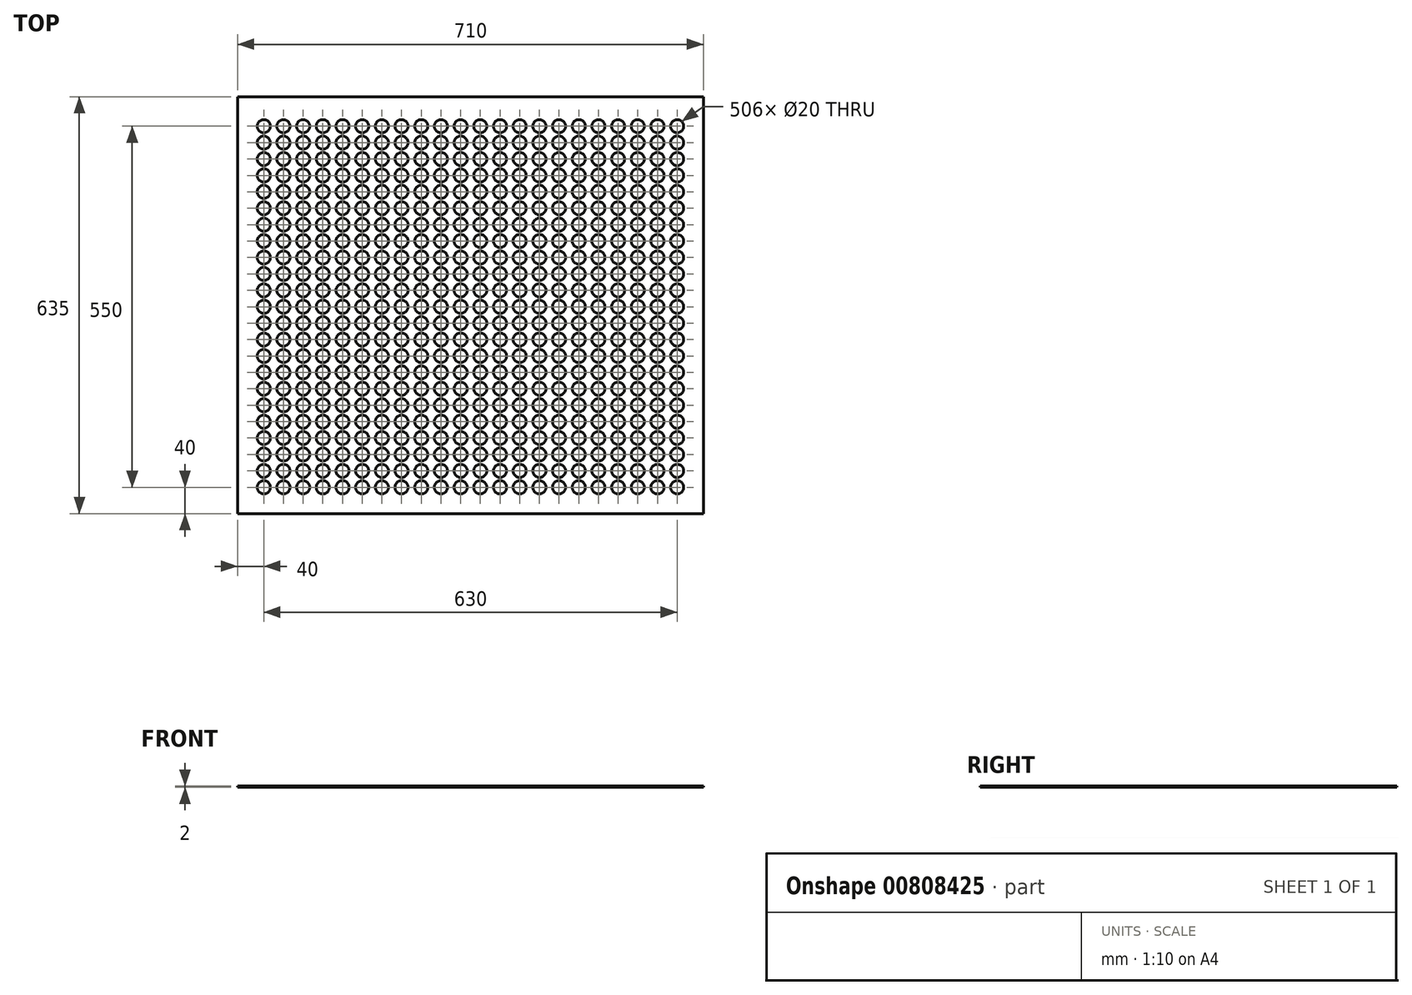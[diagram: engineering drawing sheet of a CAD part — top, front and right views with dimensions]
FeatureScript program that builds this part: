
annotation { "Feature Type Name" : "Feature", "Feature Type Description" : "" }
export const myFeature = defineFeature(function(context is Context, id is Id, definition is map)
    precondition{}
    {
        {
            var Q0;
            Q0=qCreatedBy(makeId("Top.planeOp"),FACE);
            var sketch = newSketch(context, id + "F0", { "sketchPlane" : qUnion([Q0])});
            skLineSegment(sketch, "E0.bottom", {"start": v(-355, 317.5) * mm, "end": v(355, 317.5) * mm});
            skLineSegment(sketch, "E0.top", {"start": v(-355, -317.5) * mm, "end": v(355, -317.5) * mm});
            skLineSegment(sketch, "E0.left", {"start": v(-355, 317.5) * mm, "end": v(-355, -317.5) * mm});
            skLineSegment(sketch, "E0.right", {"start": v(355, 317.5) * mm, "end": v(355, -317.5) * mm});
            skPoint(sketch, "E0.middle", {"position": v(0, 0) * mm});
            skCircle(sketch, "E1", {"center": v(-315, -277.5) * mm, "radius": 10 * mm});
            skCircle(sketch, "E2.0.1.0", {"center": v(-315, -252.5) * mm, "radius": 10 * mm});
            skCircle(sketch, "E2.0.2.0", {"center": v(-315, -227.5) * mm, "radius": 10 * mm});
            skCircle(sketch, "E2.0.3.0", {"center": v(-315, -202.5) * mm, "radius": 10 * mm});
            skCircle(sketch, "E2.0.4.0", {"center": v(-315, -177.5) * mm, "radius": 10 * mm});
            skCircle(sketch, "E2.0.5.0", {"center": v(-315, -152.5) * mm, "radius": 10 * mm});
            skCircle(sketch, "E2.0.6.0", {"center": v(-315, -127.5) * mm, "radius": 10 * mm});
            skCircle(sketch, "E2.0.7.0", {"center": v(-315, -102.5) * mm, "radius": 10 * mm});
            skCircle(sketch, "E2.0.8.0", {"center": v(-315, -77.5) * mm, "radius": 10 * mm});
            skCircle(sketch, "E2.0.9.0", {"center": v(-315, -52.5) * mm, "radius": 10 * mm});
            skCircle(sketch, "E2.1.0.0", {"center": v(-285, -277.5) * mm, "radius": 10 * mm});
            skCircle(sketch, "E2.1.1.0", {"center": v(-285, -252.5) * mm, "radius": 10 * mm});
            skCircle(sketch, "E2.1.2.0", {"center": v(-285, -227.5) * mm, "radius": 10 * mm});
            skCircle(sketch, "E2.1.3.0", {"center": v(-285, -202.5) * mm, "radius": 10 * mm});
            skCircle(sketch, "E2.1.4.0", {"center": v(-285, -177.5) * mm, "radius": 10 * mm});
            skCircle(sketch, "E2.1.5.0", {"center": v(-285, -152.5) * mm, "radius": 10 * mm});
            skCircle(sketch, "E2.1.6.0", {"center": v(-285, -127.5) * mm, "radius": 10 * mm});
            skCircle(sketch, "E2.1.7.0", {"center": v(-285, -102.5) * mm, "radius": 10 * mm});
            skCircle(sketch, "E2.1.8.0", {"center": v(-285, -77.5) * mm, "radius": 10 * mm});
            skCircle(sketch, "E2.1.9.0", {"center": v(-285, -52.5) * mm, "radius": 10 * mm});
            skCircle(sketch, "E2.2.0.0", {"center": v(-255, -277.5) * mm, "radius": 10 * mm});
            skCircle(sketch, "E2.2.1.0", {"center": v(-255, -252.5) * mm, "radius": 10 * mm});
            skCircle(sketch, "E2.2.2.0", {"center": v(-255, -227.5) * mm, "radius": 10 * mm});
            skCircle(sketch, "E2.2.3.0", {"center": v(-255, -202.5) * mm, "radius": 10 * mm});
            skCircle(sketch, "E2.2.4.0", {"center": v(-255, -177.5) * mm, "radius": 10 * mm});
            skCircle(sketch, "E2.2.5.0", {"center": v(-255, -152.5) * mm, "radius": 10 * mm});
            skCircle(sketch, "E2.2.6.0", {"center": v(-255, -127.5) * mm, "radius": 10 * mm});
            skCircle(sketch, "E2.2.7.0", {"center": v(-255, -102.5) * mm, "radius": 10 * mm});
            skCircle(sketch, "E2.2.8.0", {"center": v(-255, -77.5) * mm, "radius": 10 * mm});
            skCircle(sketch, "E2.2.9.0", {"center": v(-255, -52.5) * mm, "radius": 10 * mm});
            skCircle(sketch, "E2.3.0.0", {"center": v(-225, -277.5) * mm, "radius": 10 * mm});
            skCircle(sketch, "E2.3.1.0", {"center": v(-225, -252.5) * mm, "radius": 10 * mm});
            skCircle(sketch, "E2.3.2.0", {"center": v(-225, -227.5) * mm, "radius": 10 * mm});
            skCircle(sketch, "E2.3.3.0", {"center": v(-225, -202.5) * mm, "radius": 10 * mm});
            skCircle(sketch, "E2.3.4.0", {"center": v(-225, -177.5) * mm, "radius": 10 * mm});
            skCircle(sketch, "E2.3.5.0", {"center": v(-225, -152.5) * mm, "radius": 10 * mm});
            skCircle(sketch, "E2.3.6.0", {"center": v(-225, -127.5) * mm, "radius": 10 * mm});
            skCircle(sketch, "E2.3.7.0", {"center": v(-225, -102.5) * mm, "radius": 10 * mm});
            skCircle(sketch, "E2.3.8.0", {"center": v(-225, -77.5) * mm, "radius": 10 * mm});
            skCircle(sketch, "E2.3.9.0", {"center": v(-225, -52.5) * mm, "radius": 10 * mm});
            skCircle(sketch, "E2.4.0.0", {"center": v(-195, -277.5) * mm, "radius": 10 * mm});
            skCircle(sketch, "E2.4.1.0", {"center": v(-195, -252.5) * mm, "radius": 10 * mm});
            skCircle(sketch, "E2.4.2.0", {"center": v(-195, -227.5) * mm, "radius": 10 * mm});
            skCircle(sketch, "E2.4.3.0", {"center": v(-195, -202.5) * mm, "radius": 10 * mm});
            skCircle(sketch, "E2.4.4.0", {"center": v(-195, -177.5) * mm, "radius": 10 * mm});
            skCircle(sketch, "E2.4.5.0", {"center": v(-195, -152.5) * mm, "radius": 10 * mm});
            skCircle(sketch, "E2.4.6.0", {"center": v(-195, -127.5) * mm, "radius": 10 * mm});
            skCircle(sketch, "E2.4.7.0", {"center": v(-195, -102.5) * mm, "radius": 10 * mm});
            skCircle(sketch, "E2.4.8.0", {"center": v(-195, -77.5) * mm, "radius": 10 * mm});
            skCircle(sketch, "E2.4.9.0", {"center": v(-195, -52.5) * mm, "radius": 10 * mm});
            skCircle(sketch, "E2.5.0.0", {"center": v(-165, -277.5) * mm, "radius": 10 * mm});
            skCircle(sketch, "E2.5.1.0", {"center": v(-165, -252.5) * mm, "radius": 10 * mm});
            skCircle(sketch, "E2.5.2.0", {"center": v(-165, -227.5) * mm, "radius": 10 * mm});
            skCircle(sketch, "E2.5.3.0", {"center": v(-165, -202.5) * mm, "radius": 10 * mm});
            skCircle(sketch, "E2.5.4.0", {"center": v(-165, -177.5) * mm, "radius": 10 * mm});
            skCircle(sketch, "E2.5.5.0", {"center": v(-165, -152.5) * mm, "radius": 10 * mm});
            skCircle(sketch, "E2.5.6.0", {"center": v(-165, -127.5) * mm, "radius": 10 * mm});
            skCircle(sketch, "E2.5.7.0", {"center": v(-165, -102.5) * mm, "radius": 10 * mm});
            skCircle(sketch, "E2.5.8.0", {"center": v(-165, -77.5) * mm, "radius": 10 * mm});
            skCircle(sketch, "E2.5.9.0", {"center": v(-165, -52.5) * mm, "radius": 10 * mm});
            skCircle(sketch, "E2.6.0.0", {"center": v(-135, -277.5) * mm, "radius": 10 * mm});
            skCircle(sketch, "E2.6.1.0", {"center": v(-135, -252.5) * mm, "radius": 10 * mm});
            skCircle(sketch, "E2.6.2.0", {"center": v(-135, -227.5) * mm, "radius": 10 * mm});
            skCircle(sketch, "E2.6.3.0", {"center": v(-135, -202.5) * mm, "radius": 10 * mm});
            skCircle(sketch, "E2.6.4.0", {"center": v(-135, -177.5) * mm, "radius": 10 * mm});
            skCircle(sketch, "E2.6.5.0", {"center": v(-135, -152.5) * mm, "radius": 10 * mm});
            skCircle(sketch, "E2.6.6.0", {"center": v(-135, -127.5) * mm, "radius": 10 * mm});
            skCircle(sketch, "E2.6.7.0", {"center": v(-135, -102.5) * mm, "radius": 10 * mm});
            skCircle(sketch, "E2.6.8.0", {"center": v(-135, -77.5) * mm, "radius": 10 * mm});
            skCircle(sketch, "E2.6.9.0", {"center": v(-135, -52.5) * mm, "radius": 10 * mm});
            skCircle(sketch, "E2.7.0.0", {"center": v(-105, -277.5) * mm, "radius": 10 * mm});
            skCircle(sketch, "E2.7.1.0", {"center": v(-105, -252.5) * mm, "radius": 10 * mm});
            skCircle(sketch, "E2.7.2.0", {"center": v(-105, -227.5) * mm, "radius": 10 * mm});
            skCircle(sketch, "E2.7.3.0", {"center": v(-105, -202.5) * mm, "radius": 10 * mm});
            skCircle(sketch, "E2.7.4.0", {"center": v(-105, -177.5) * mm, "radius": 10 * mm});
            skCircle(sketch, "E2.7.5.0", {"center": v(-105, -152.5) * mm, "radius": 10 * mm});
            skCircle(sketch, "E2.7.6.0", {"center": v(-105, -127.5) * mm, "radius": 10 * mm});
            skCircle(sketch, "E2.7.7.0", {"center": v(-105, -102.5) * mm, "radius": 10 * mm});
            skCircle(sketch, "E2.7.8.0", {"center": v(-105, -77.5) * mm, "radius": 10 * mm});
            skCircle(sketch, "E2.7.9.0", {"center": v(-105, -52.5) * mm, "radius": 10 * mm});
            skCircle(sketch, "E2.8.0.0", {"center": v(-75, -277.5) * mm, "radius": 10 * mm});
            skCircle(sketch, "E2.8.1.0", {"center": v(-75, -252.5) * mm, "radius": 10 * mm});
            skCircle(sketch, "E2.8.2.0", {"center": v(-75, -227.5) * mm, "radius": 10 * mm});
            skCircle(sketch, "E2.8.3.0", {"center": v(-75, -202.5) * mm, "radius": 10 * mm});
            skCircle(sketch, "E2.8.4.0", {"center": v(-75, -177.5) * mm, "radius": 10 * mm});
            skCircle(sketch, "E2.8.5.0", {"center": v(-75, -152.5) * mm, "radius": 10 * mm});
            skCircle(sketch, "E2.8.6.0", {"center": v(-75, -127.5) * mm, "radius": 10 * mm});
            skCircle(sketch, "E2.8.7.0", {"center": v(-75, -102.5) * mm, "radius": 10 * mm});
            skCircle(sketch, "E2.8.8.0", {"center": v(-75, -77.5) * mm, "radius": 10 * mm});
            skCircle(sketch, "E2.8.9.0", {"center": v(-75, -52.5) * mm, "radius": 10 * mm});
            skCircle(sketch, "E2.9.0.0", {"center": v(-45, -277.5) * mm, "radius": 10 * mm});
            skCircle(sketch, "E2.9.1.0", {"center": v(-45, -252.5) * mm, "radius": 10 * mm});
            skCircle(sketch, "E2.9.2.0", {"center": v(-45, -227.5) * mm, "radius": 10 * mm});
            skCircle(sketch, "E2.9.3.0", {"center": v(-45, -202.5) * mm, "radius": 10 * mm});
            skCircle(sketch, "E2.9.4.0", {"center": v(-45, -177.5) * mm, "radius": 10 * mm});
            skCircle(sketch, "E2.9.5.0", {"center": v(-45, -152.5) * mm, "radius": 10 * mm});
            skCircle(sketch, "E2.9.6.0", {"center": v(-45, -127.5) * mm, "radius": 10 * mm});
            skCircle(sketch, "E2.9.7.0", {"center": v(-45, -102.5) * mm, "radius": 10 * mm});
            skCircle(sketch, "E2.9.8.0", {"center": v(-45, -77.5) * mm, "radius": 10 * mm});
            skCircle(sketch, "E2.9.9.0", {"center": v(-45, -52.5) * mm, "radius": 10 * mm});
            skCircle(sketch, "E2.10.0.0", {"center": v(-15, -277.5) * mm, "radius": 10 * mm});
            skCircle(sketch, "E2.10.1.0", {"center": v(-15, -252.5) * mm, "radius": 10 * mm});
            skCircle(sketch, "E2.10.2.0", {"center": v(-15, -227.5) * mm, "radius": 10 * mm});
            skCircle(sketch, "E2.10.3.0", {"center": v(-15, -202.5) * mm, "radius": 10 * mm});
            skCircle(sketch, "E2.10.4.0", {"center": v(-15, -177.5) * mm, "radius": 10 * mm});
            skCircle(sketch, "E2.10.5.0", {"center": v(-15, -152.5) * mm, "radius": 10 * mm});
            skCircle(sketch, "E2.10.6.0", {"center": v(-15, -127.5) * mm, "radius": 10 * mm});
            skCircle(sketch, "E2.10.7.0", {"center": v(-15, -102.5) * mm, "radius": 10 * mm});
            skCircle(sketch, "E2.10.8.0", {"center": v(-15, -77.5) * mm, "radius": 10 * mm});
            skCircle(sketch, "E2.10.9.0", {"center": v(-15, -52.5) * mm, "radius": 10 * mm});
            skCircle(sketch, "E2.11.0.0", {"center": v(15, -277.5) * mm, "radius": 10 * mm});
            skCircle(sketch, "E2.11.1.0", {"center": v(15, -252.5) * mm, "radius": 10 * mm});
            skCircle(sketch, "E2.11.2.0", {"center": v(15, -227.5) * mm, "radius": 10 * mm});
            skCircle(sketch, "E2.11.3.0", {"center": v(15, -202.5) * mm, "radius": 10 * mm});
            skCircle(sketch, "E2.11.4.0", {"center": v(15, -177.5) * mm, "radius": 10 * mm});
            skCircle(sketch, "E2.11.5.0", {"center": v(15, -152.5) * mm, "radius": 10 * mm});
            skCircle(sketch, "E2.11.6.0", {"center": v(15, -127.5) * mm, "radius": 10 * mm});
            skCircle(sketch, "E2.11.7.0", {"center": v(15, -102.5) * mm, "radius": 10 * mm});
            skCircle(sketch, "E2.11.8.0", {"center": v(15, -77.5) * mm, "radius": 10 * mm});
            skCircle(sketch, "E2.11.9.0", {"center": v(15, -52.5) * mm, "radius": 10 * mm});
            skCircle(sketch, "E2.12.0.0", {"center": v(45, -277.5) * mm, "radius": 10 * mm});
            skCircle(sketch, "E2.12.1.0", {"center": v(45, -252.5) * mm, "radius": 10 * mm});
            skCircle(sketch, "E2.12.2.0", {"center": v(45, -227.5) * mm, "radius": 10 * mm});
            skCircle(sketch, "E2.12.3.0", {"center": v(45, -202.5) * mm, "radius": 10 * mm});
            skCircle(sketch, "E2.12.4.0", {"center": v(45, -177.5) * mm, "radius": 10 * mm});
            skCircle(sketch, "E2.12.5.0", {"center": v(45, -152.5) * mm, "radius": 10 * mm});
            skCircle(sketch, "E2.12.6.0", {"center": v(45, -127.5) * mm, "radius": 10 * mm});
            skCircle(sketch, "E2.12.7.0", {"center": v(45, -102.5) * mm, "radius": 10 * mm});
            skCircle(sketch, "E2.12.8.0", {"center": v(45, -77.5) * mm, "radius": 10 * mm});
            skCircle(sketch, "E2.12.9.0", {"center": v(45, -52.5) * mm, "radius": 10 * mm});
            skCircle(sketch, "E2.13.0.0", {"center": v(75, -277.5) * mm, "radius": 10 * mm});
            skCircle(sketch, "E2.13.1.0", {"center": v(75, -252.5) * mm, "radius": 10 * mm});
            skCircle(sketch, "E2.13.2.0", {"center": v(75, -227.5) * mm, "radius": 10 * mm});
            skCircle(sketch, "E2.13.3.0", {"center": v(75, -202.5) * mm, "radius": 10 * mm});
            skCircle(sketch, "E2.13.4.0", {"center": v(75, -177.5) * mm, "radius": 10 * mm});
            skCircle(sketch, "E2.13.5.0", {"center": v(75, -152.5) * mm, "radius": 10 * mm});
            skCircle(sketch, "E2.13.6.0", {"center": v(75, -127.5) * mm, "radius": 10 * mm});
            skCircle(sketch, "E2.13.7.0", {"center": v(75, -102.5) * mm, "radius": 10 * mm});
            skCircle(sketch, "E2.13.8.0", {"center": v(75, -77.5) * mm, "radius": 10 * mm});
            skCircle(sketch, "E2.13.9.0", {"center": v(75, -52.5) * mm, "radius": 10 * mm});
            skCircle(sketch, "E2.14.0.0", {"center": v(105, -277.5) * mm, "radius": 10 * mm});
            skCircle(sketch, "E2.14.1.0", {"center": v(105, -252.5) * mm, "radius": 10 * mm});
            skCircle(sketch, "E2.14.2.0", {"center": v(105, -227.5) * mm, "radius": 10 * mm});
            skCircle(sketch, "E2.14.3.0", {"center": v(105, -202.5) * mm, "radius": 10 * mm});
            skCircle(sketch, "E2.14.4.0", {"center": v(105, -177.5) * mm, "radius": 10 * mm});
            skCircle(sketch, "E2.14.5.0", {"center": v(105, -152.5) * mm, "radius": 10 * mm});
            skCircle(sketch, "E2.14.6.0", {"center": v(105, -127.5) * mm, "radius": 10 * mm});
            skCircle(sketch, "E2.14.7.0", {"center": v(105, -102.5) * mm, "radius": 10 * mm});
            skCircle(sketch, "E2.14.8.0", {"center": v(105, -77.5) * mm, "radius": 10 * mm});
            skCircle(sketch, "E2.14.9.0", {"center": v(105, -52.5) * mm, "radius": 10 * mm});
            skCircle(sketch, "E2.15.0.0", {"center": v(135, -277.5) * mm, "radius": 10 * mm});
            skCircle(sketch, "E2.15.1.0", {"center": v(135, -252.5) * mm, "radius": 10 * mm});
            skCircle(sketch, "E2.15.2.0", {"center": v(135, -227.5) * mm, "radius": 10 * mm});
            skCircle(sketch, "E2.15.3.0", {"center": v(135, -202.5) * mm, "radius": 10 * mm});
            skCircle(sketch, "E2.15.4.0", {"center": v(135, -177.5) * mm, "radius": 10 * mm});
            skCircle(sketch, "E2.15.5.0", {"center": v(135, -152.5) * mm, "radius": 10 * mm});
            skCircle(sketch, "E2.15.6.0", {"center": v(135, -127.5) * mm, "radius": 10 * mm});
            skCircle(sketch, "E2.15.7.0", {"center": v(135, -102.5) * mm, "radius": 10 * mm});
            skCircle(sketch, "E2.15.8.0", {"center": v(135, -77.5) * mm, "radius": 10 * mm});
            skCircle(sketch, "E2.15.9.0", {"center": v(135, -52.5) * mm, "radius": 10 * mm});
            skCircle(sketch, "E2.16.0.0", {"center": v(165, -277.5) * mm, "radius": 10 * mm});
            skCircle(sketch, "E2.16.1.0", {"center": v(165, -252.5) * mm, "radius": 10 * mm});
            skCircle(sketch, "E2.16.2.0", {"center": v(165, -227.5) * mm, "radius": 10 * mm});
            skCircle(sketch, "E2.16.3.0", {"center": v(165, -202.5) * mm, "radius": 10 * mm});
            skCircle(sketch, "E2.16.4.0", {"center": v(165, -177.5) * mm, "radius": 10 * mm});
            skCircle(sketch, "E2.16.5.0", {"center": v(165, -152.5) * mm, "radius": 10 * mm});
            skCircle(sketch, "E2.16.6.0", {"center": v(165, -127.5) * mm, "radius": 10 * mm});
            skCircle(sketch, "E2.16.7.0", {"center": v(165, -102.5) * mm, "radius": 10 * mm});
            skCircle(sketch, "E2.16.8.0", {"center": v(165, -77.5) * mm, "radius": 10 * mm});
            skCircle(sketch, "E2.16.9.0", {"center": v(165, -52.5) * mm, "radius": 10 * mm});
            skCircle(sketch, "E2.17.0.0", {"center": v(195, -277.5) * mm, "radius": 10 * mm});
            skCircle(sketch, "E2.17.1.0", {"center": v(195, -252.5) * mm, "radius": 10 * mm});
            skCircle(sketch, "E2.17.2.0", {"center": v(195, -227.5) * mm, "radius": 10 * mm});
            skCircle(sketch, "E2.17.3.0", {"center": v(195, -202.5) * mm, "radius": 10 * mm});
            skCircle(sketch, "E2.17.4.0", {"center": v(195, -177.5) * mm, "radius": 10 * mm});
            skCircle(sketch, "E2.17.5.0", {"center": v(195, -152.5) * mm, "radius": 10 * mm});
            skCircle(sketch, "E2.17.6.0", {"center": v(195, -127.5) * mm, "radius": 10 * mm});
            skCircle(sketch, "E2.17.7.0", {"center": v(195, -102.5) * mm, "radius": 10 * mm});
            skCircle(sketch, "E2.17.8.0", {"center": v(195, -77.5) * mm, "radius": 10 * mm});
            skCircle(sketch, "E2.17.9.0", {"center": v(195, -52.5) * mm, "radius": 10 * mm});
            skCircle(sketch, "E2.18.0.0", {"center": v(225, -277.5) * mm, "radius": 10 * mm});
            skCircle(sketch, "E2.18.1.0", {"center": v(225, -252.5) * mm, "radius": 10 * mm});
            skCircle(sketch, "E2.18.2.0", {"center": v(225, -227.5) * mm, "radius": 10 * mm});
            skCircle(sketch, "E2.18.3.0", {"center": v(225, -202.5) * mm, "radius": 10 * mm});
            skCircle(sketch, "E2.18.4.0", {"center": v(225, -177.5) * mm, "radius": 10 * mm});
            skCircle(sketch, "E2.18.5.0", {"center": v(225, -152.5) * mm, "radius": 10 * mm});
            skCircle(sketch, "E2.18.6.0", {"center": v(225, -127.5) * mm, "radius": 10 * mm});
            skCircle(sketch, "E2.18.7.0", {"center": v(225, -102.5) * mm, "radius": 10 * mm});
            skCircle(sketch, "E2.18.8.0", {"center": v(225, -77.5) * mm, "radius": 10 * mm});
            skCircle(sketch, "E2.18.9.0", {"center": v(225, -52.5) * mm, "radius": 10 * mm});
            skCircle(sketch, "E2.19.0.0", {"center": v(255, -277.5) * mm, "radius": 10 * mm});
            skCircle(sketch, "E2.19.1.0", {"center": v(255, -252.5) * mm, "radius": 10 * mm});
            skCircle(sketch, "E2.19.2.0", {"center": v(255, -227.5) * mm, "radius": 10 * mm});
            skCircle(sketch, "E2.19.3.0", {"center": v(255, -202.5) * mm, "radius": 10 * mm});
            skCircle(sketch, "E2.19.4.0", {"center": v(255, -177.5) * mm, "radius": 10 * mm});
            skCircle(sketch, "E2.19.5.0", {"center": v(255, -152.5) * mm, "radius": 10 * mm});
            skCircle(sketch, "E2.19.6.0", {"center": v(255, -127.5) * mm, "radius": 10 * mm});
            skCircle(sketch, "E2.19.7.0", {"center": v(255, -102.5) * mm, "radius": 10 * mm});
            skCircle(sketch, "E2.19.8.0", {"center": v(255, -77.5) * mm, "radius": 10 * mm});
            skCircle(sketch, "E2.19.9.0", {"center": v(255, -52.5) * mm, "radius": 10 * mm});
            skLineSegment(sketch, "E2.direction1", {"start": v(-315, -277.5) * mm, "end": v(-285, -277.5) * mm, "construction": true});
            skLineSegment(sketch, "E2.direction2", {"start": v(-315, -277.5) * mm, "end": v(-315, -252.5) * mm, "construction": true});
            skCircle(sketch, "E3.0.0.10", {"center": v(-315, -27.5) * mm, "radius": 10 * mm});
            skCircle(sketch, "E3.0.0.11", {"center": v(-315, -2.5) * mm, "radius": 10 * mm});
            skCircle(sketch, "E3.0.0.12", {"center": v(-315, 22.5) * mm, "radius": 10 * mm});
            skCircle(sketch, "E3.0.0.13", {"center": v(-315, 47.5) * mm, "radius": 10 * mm});
            skCircle(sketch, "E3.0.0.14", {"center": v(-315, 72.5) * mm, "radius": 10 * mm});
            skCircle(sketch, "E3.0.0.15", {"center": v(-315, 97.5) * mm, "radius": 10 * mm});
            skCircle(sketch, "E3.0.0.16", {"center": v(-315, 122.5) * mm, "radius": 10 * mm});
            skCircle(sketch, "E3.0.0.17", {"center": v(-315, 147.5) * mm, "radius": 10 * mm});
            skCircle(sketch, "E3.0.0.18", {"center": v(-315, 172.5) * mm, "radius": 10 * mm});
            skCircle(sketch, "E3.0.0.19", {"center": v(-315, 197.5) * mm, "radius": 10 * mm});
            skCircle(sketch, "E3.0.0.20", {"center": v(-315, 222.5) * mm, "radius": 10 * mm});
            skCircle(sketch, "E3.0.0.21", {"center": v(-315, 247.5) * mm, "radius": 10 * mm});
            skCircle(sketch, "E3.0.0.22", {"center": v(-315, 272.5) * mm, "radius": 10 * mm});
            skCircle(sketch, "E3.0.1.10", {"center": v(-285, -27.5) * mm, "radius": 10 * mm});
            skCircle(sketch, "E3.0.1.11", {"center": v(-285, -2.5) * mm, "radius": 10 * mm});
            skCircle(sketch, "E3.0.1.12", {"center": v(-285, 22.5) * mm, "radius": 10 * mm});
            skCircle(sketch, "E3.0.1.13", {"center": v(-285, 47.5) * mm, "radius": 10 * mm});
            skCircle(sketch, "E3.0.1.14", {"center": v(-285, 72.5) * mm, "radius": 10 * mm});
            skCircle(sketch, "E3.0.1.15", {"center": v(-285, 97.5) * mm, "radius": 10 * mm});
            skCircle(sketch, "E3.0.1.16", {"center": v(-285, 122.5) * mm, "radius": 10 * mm});
            skCircle(sketch, "E3.0.1.17", {"center": v(-285, 147.5) * mm, "radius": 10 * mm});
            skCircle(sketch, "E3.0.1.18", {"center": v(-285, 172.5) * mm, "radius": 10 * mm});
            skCircle(sketch, "E3.0.1.19", {"center": v(-285, 197.5) * mm, "radius": 10 * mm});
            skCircle(sketch, "E3.0.1.20", {"center": v(-285, 222.5) * mm, "radius": 10 * mm});
            skCircle(sketch, "E3.0.1.21", {"center": v(-285, 247.5) * mm, "radius": 10 * mm});
            skCircle(sketch, "E3.0.1.22", {"center": v(-285, 272.5) * mm, "radius": 10 * mm});
            skCircle(sketch, "E3.0.2.10", {"center": v(-255, -27.5) * mm, "radius": 10 * mm});
            skCircle(sketch, "E3.0.2.11", {"center": v(-255, -2.5) * mm, "radius": 10 * mm});
            skCircle(sketch, "E3.0.2.12", {"center": v(-255, 22.5) * mm, "radius": 10 * mm});
            skCircle(sketch, "E3.0.2.13", {"center": v(-255, 47.5) * mm, "radius": 10 * mm});
            skCircle(sketch, "E3.0.2.14", {"center": v(-255, 72.5) * mm, "radius": 10 * mm});
            skCircle(sketch, "E3.0.2.15", {"center": v(-255, 97.5) * mm, "radius": 10 * mm});
            skCircle(sketch, "E3.0.2.16", {"center": v(-255, 122.5) * mm, "radius": 10 * mm});
            skCircle(sketch, "E3.0.2.17", {"center": v(-255, 147.5) * mm, "radius": 10 * mm});
            skCircle(sketch, "E3.0.2.18", {"center": v(-255, 172.5) * mm, "radius": 10 * mm});
            skCircle(sketch, "E3.0.2.19", {"center": v(-255, 197.5) * mm, "radius": 10 * mm});
            skCircle(sketch, "E3.0.2.20", {"center": v(-255, 222.5) * mm, "radius": 10 * mm});
            skCircle(sketch, "E3.0.2.21", {"center": v(-255, 247.5) * mm, "radius": 10 * mm});
            skCircle(sketch, "E3.0.2.22", {"center": v(-255, 272.5) * mm, "radius": 10 * mm});
            skCircle(sketch, "E3.0.3.10", {"center": v(-225, -27.5) * mm, "radius": 10 * mm});
            skCircle(sketch, "E3.0.3.11", {"center": v(-225, -2.5) * mm, "radius": 10 * mm});
            skCircle(sketch, "E3.0.3.12", {"center": v(-225, 22.5) * mm, "radius": 10 * mm});
            skCircle(sketch, "E3.0.3.13", {"center": v(-225, 47.5) * mm, "radius": 10 * mm});
            skCircle(sketch, "E3.0.3.14", {"center": v(-225, 72.5) * mm, "radius": 10 * mm});
            skCircle(sketch, "E3.0.3.15", {"center": v(-225, 97.5) * mm, "radius": 10 * mm});
            skCircle(sketch, "E3.0.3.16", {"center": v(-225, 122.5) * mm, "radius": 10 * mm});
            skCircle(sketch, "E3.0.3.17", {"center": v(-225, 147.5) * mm, "radius": 10 * mm});
            skCircle(sketch, "E3.0.3.18", {"center": v(-225, 172.5) * mm, "radius": 10 * mm});
            skCircle(sketch, "E3.0.3.19", {"center": v(-225, 197.5) * mm, "radius": 10 * mm});
            skCircle(sketch, "E3.0.3.20", {"center": v(-225, 222.5) * mm, "radius": 10 * mm});
            skCircle(sketch, "E3.0.3.21", {"center": v(-225, 247.5) * mm, "radius": 10 * mm});
            skCircle(sketch, "E3.0.3.22", {"center": v(-225, 272.5) * mm, "radius": 10 * mm});
            skCircle(sketch, "E3.0.4.10", {"center": v(-195, -27.5) * mm, "radius": 10 * mm});
            skCircle(sketch, "E3.0.4.11", {"center": v(-195, -2.5) * mm, "radius": 10 * mm});
            skCircle(sketch, "E3.0.4.12", {"center": v(-195, 22.5) * mm, "radius": 10 * mm});
            skCircle(sketch, "E3.0.4.13", {"center": v(-195, 47.5) * mm, "radius": 10 * mm});
            skCircle(sketch, "E3.0.4.14", {"center": v(-195, 72.5) * mm, "radius": 10 * mm});
            skCircle(sketch, "E3.0.4.15", {"center": v(-195, 97.5) * mm, "radius": 10 * mm});
            skCircle(sketch, "E3.0.4.16", {"center": v(-195, 122.5) * mm, "radius": 10 * mm});
            skCircle(sketch, "E3.0.4.17", {"center": v(-195, 147.5) * mm, "radius": 10 * mm});
            skCircle(sketch, "E3.0.4.18", {"center": v(-195, 172.5) * mm, "radius": 10 * mm});
            skCircle(sketch, "E3.0.4.19", {"center": v(-195, 197.5) * mm, "radius": 10 * mm});
            skCircle(sketch, "E3.0.4.20", {"center": v(-195, 222.5) * mm, "radius": 10 * mm});
            skCircle(sketch, "E3.0.4.21", {"center": v(-195, 247.5) * mm, "radius": 10 * mm});
            skCircle(sketch, "E3.0.4.22", {"center": v(-195, 272.5) * mm, "radius": 10 * mm});
            skCircle(sketch, "E3.0.5.10", {"center": v(-165, -27.5) * mm, "radius": 10 * mm});
            skCircle(sketch, "E3.0.5.11", {"center": v(-165, -2.5) * mm, "radius": 10 * mm});
            skCircle(sketch, "E3.0.5.12", {"center": v(-165, 22.5) * mm, "radius": 10 * mm});
            skCircle(sketch, "E3.0.5.13", {"center": v(-165, 47.5) * mm, "radius": 10 * mm});
            skCircle(sketch, "E3.0.5.14", {"center": v(-165, 72.5) * mm, "radius": 10 * mm});
            skCircle(sketch, "E3.0.5.15", {"center": v(-165, 97.5) * mm, "radius": 10 * mm});
            skCircle(sketch, "E3.0.5.16", {"center": v(-165, 122.5) * mm, "radius": 10 * mm});
            skCircle(sketch, "E3.0.5.17", {"center": v(-165, 147.5) * mm, "radius": 10 * mm});
            skCircle(sketch, "E3.0.5.18", {"center": v(-165, 172.5) * mm, "radius": 10 * mm});
            skCircle(sketch, "E3.0.5.19", {"center": v(-165, 197.5) * mm, "radius": 10 * mm});
            skCircle(sketch, "E3.0.5.20", {"center": v(-165, 222.5) * mm, "radius": 10 * mm});
            skCircle(sketch, "E3.0.5.21", {"center": v(-165, 247.5) * mm, "radius": 10 * mm});
            skCircle(sketch, "E3.0.5.22", {"center": v(-165, 272.5) * mm, "radius": 10 * mm});
            skCircle(sketch, "E3.0.6.10", {"center": v(-135, -27.5) * mm, "radius": 10 * mm});
            skCircle(sketch, "E3.0.6.11", {"center": v(-135, -2.5) * mm, "radius": 10 * mm});
            skCircle(sketch, "E3.0.6.12", {"center": v(-135, 22.5) * mm, "radius": 10 * mm});
            skCircle(sketch, "E3.0.6.13", {"center": v(-135, 47.5) * mm, "radius": 10 * mm});
            skCircle(sketch, "E3.0.6.14", {"center": v(-135, 72.5) * mm, "radius": 10 * mm});
            skCircle(sketch, "E3.0.6.15", {"center": v(-135, 97.5) * mm, "radius": 10 * mm});
            skCircle(sketch, "E3.0.6.16", {"center": v(-135, 122.5) * mm, "radius": 10 * mm});
            skCircle(sketch, "E3.0.6.17", {"center": v(-135, 147.5) * mm, "radius": 10 * mm});
            skCircle(sketch, "E3.0.6.18", {"center": v(-135, 172.5) * mm, "radius": 10 * mm});
            skCircle(sketch, "E3.0.6.19", {"center": v(-135, 197.5) * mm, "radius": 10 * mm});
            skCircle(sketch, "E3.0.6.20", {"center": v(-135, 222.5) * mm, "radius": 10 * mm});
            skCircle(sketch, "E3.0.6.21", {"center": v(-135, 247.5) * mm, "radius": 10 * mm});
            skCircle(sketch, "E3.0.6.22", {"center": v(-135, 272.5) * mm, "radius": 10 * mm});
            skCircle(sketch, "E3.0.7.10", {"center": v(-105, -27.5) * mm, "radius": 10 * mm});
            skCircle(sketch, "E3.0.7.11", {"center": v(-105, -2.5) * mm, "radius": 10 * mm});
            skCircle(sketch, "E3.0.7.12", {"center": v(-105, 22.5) * mm, "radius": 10 * mm});
            skCircle(sketch, "E3.0.7.13", {"center": v(-105, 47.5) * mm, "radius": 10 * mm});
            skCircle(sketch, "E3.0.7.14", {"center": v(-105, 72.5) * mm, "radius": 10 * mm});
            skCircle(sketch, "E3.0.7.15", {"center": v(-105, 97.5) * mm, "radius": 10 * mm});
            skCircle(sketch, "E3.0.7.16", {"center": v(-105, 122.5) * mm, "radius": 10 * mm});
            skCircle(sketch, "E3.0.7.17", {"center": v(-105, 147.5) * mm, "radius": 10 * mm});
            skCircle(sketch, "E3.0.7.18", {"center": v(-105, 172.5) * mm, "radius": 10 * mm});
            skCircle(sketch, "E3.0.7.19", {"center": v(-105, 197.5) * mm, "radius": 10 * mm});
            skCircle(sketch, "E3.0.7.20", {"center": v(-105, 222.5) * mm, "radius": 10 * mm});
            skCircle(sketch, "E3.0.7.21", {"center": v(-105, 247.5) * mm, "radius": 10 * mm});
            skCircle(sketch, "E3.0.7.22", {"center": v(-105, 272.5) * mm, "radius": 10 * mm});
            skCircle(sketch, "E3.0.8.10", {"center": v(-75, -27.5) * mm, "radius": 10 * mm});
            skCircle(sketch, "E3.0.8.11", {"center": v(-75, -2.5) * mm, "radius": 10 * mm});
            skCircle(sketch, "E3.0.8.12", {"center": v(-75, 22.5) * mm, "radius": 10 * mm});
            skCircle(sketch, "E3.0.8.13", {"center": v(-75, 47.5) * mm, "radius": 10 * mm});
            skCircle(sketch, "E3.0.8.14", {"center": v(-75, 72.5) * mm, "radius": 10 * mm});
            skCircle(sketch, "E3.0.8.15", {"center": v(-75, 97.5) * mm, "radius": 10 * mm});
            skCircle(sketch, "E3.0.8.16", {"center": v(-75, 122.5) * mm, "radius": 10 * mm});
            skCircle(sketch, "E3.0.8.17", {"center": v(-75, 147.5) * mm, "radius": 10 * mm});
            skCircle(sketch, "E3.0.8.18", {"center": v(-75, 172.5) * mm, "radius": 10 * mm});
            skCircle(sketch, "E3.0.8.19", {"center": v(-75, 197.5) * mm, "radius": 10 * mm});
            skCircle(sketch, "E3.0.8.20", {"center": v(-75, 222.5) * mm, "radius": 10 * mm});
            skCircle(sketch, "E3.0.8.21", {"center": v(-75, 247.5) * mm, "radius": 10 * mm});
            skCircle(sketch, "E3.0.8.22", {"center": v(-75, 272.5) * mm, "radius": 10 * mm});
            skCircle(sketch, "E3.0.9.10", {"center": v(-45, -27.5) * mm, "radius": 10 * mm});
            skCircle(sketch, "E3.0.9.11", {"center": v(-45, -2.5) * mm, "radius": 10 * mm});
            skCircle(sketch, "E3.0.9.12", {"center": v(-45, 22.5) * mm, "radius": 10 * mm});
            skCircle(sketch, "E3.0.9.13", {"center": v(-45, 47.5) * mm, "radius": 10 * mm});
            skCircle(sketch, "E3.0.9.14", {"center": v(-45, 72.5) * mm, "radius": 10 * mm});
            skCircle(sketch, "E3.0.9.15", {"center": v(-45, 97.5) * mm, "radius": 10 * mm});
            skCircle(sketch, "E3.0.9.16", {"center": v(-45, 122.5) * mm, "radius": 10 * mm});
            skCircle(sketch, "E3.0.9.17", {"center": v(-45, 147.5) * mm, "radius": 10 * mm});
            skCircle(sketch, "E3.0.9.18", {"center": v(-45, 172.5) * mm, "radius": 10 * mm});
            skCircle(sketch, "E3.0.9.19", {"center": v(-45, 197.5) * mm, "radius": 10 * mm});
            skCircle(sketch, "E3.0.9.20", {"center": v(-45, 222.5) * mm, "radius": 10 * mm});
            skCircle(sketch, "E3.0.9.21", {"center": v(-45, 247.5) * mm, "radius": 10 * mm});
            skCircle(sketch, "E3.0.9.22", {"center": v(-45, 272.5) * mm, "radius": 10 * mm});
            skCircle(sketch, "E3.0.10.10", {"center": v(-15, -27.5) * mm, "radius": 10 * mm});
            skCircle(sketch, "E3.0.10.11", {"center": v(-15, -2.5) * mm, "radius": 10 * mm});
            skCircle(sketch, "E3.0.10.12", {"center": v(-15, 22.5) * mm, "radius": 10 * mm});
            skCircle(sketch, "E3.0.10.13", {"center": v(-15, 47.5) * mm, "radius": 10 * mm});
            skCircle(sketch, "E3.0.10.14", {"center": v(-15, 72.5) * mm, "radius": 10 * mm});
            skCircle(sketch, "E3.0.10.15", {"center": v(-15, 97.5) * mm, "radius": 10 * mm});
            skCircle(sketch, "E3.0.10.16", {"center": v(-15, 122.5) * mm, "radius": 10 * mm});
            skCircle(sketch, "E3.0.10.17", {"center": v(-15, 147.5) * mm, "radius": 10 * mm});
            skCircle(sketch, "E3.0.10.18", {"center": v(-15, 172.5) * mm, "radius": 10 * mm});
            skCircle(sketch, "E3.0.10.19", {"center": v(-15, 197.5) * mm, "radius": 10 * mm});
            skCircle(sketch, "E3.0.10.20", {"center": v(-15, 222.5) * mm, "radius": 10 * mm});
            skCircle(sketch, "E3.0.10.21", {"center": v(-15, 247.5) * mm, "radius": 10 * mm});
            skCircle(sketch, "E3.0.10.22", {"center": v(-15, 272.5) * mm, "radius": 10 * mm});
            skCircle(sketch, "E3.0.11.10", {"center": v(15, -27.5) * mm, "radius": 10 * mm});
            skCircle(sketch, "E3.0.11.11", {"center": v(15, -2.5) * mm, "radius": 10 * mm});
            skCircle(sketch, "E3.0.11.12", {"center": v(15, 22.5) * mm, "radius": 10 * mm});
            skCircle(sketch, "E3.0.11.13", {"center": v(15, 47.5) * mm, "radius": 10 * mm});
            skCircle(sketch, "E3.0.11.14", {"center": v(15, 72.5) * mm, "radius": 10 * mm});
            skCircle(sketch, "E3.0.11.15", {"center": v(15, 97.5) * mm, "radius": 10 * mm});
            skCircle(sketch, "E3.0.11.16", {"center": v(15, 122.5) * mm, "radius": 10 * mm});
            skCircle(sketch, "E3.0.11.17", {"center": v(15, 147.5) * mm, "radius": 10 * mm});
            skCircle(sketch, "E3.0.11.18", {"center": v(15, 172.5) * mm, "radius": 10 * mm});
            skCircle(sketch, "E3.0.11.19", {"center": v(15, 197.5) * mm, "radius": 10 * mm});
            skCircle(sketch, "E3.0.11.20", {"center": v(15, 222.5) * mm, "radius": 10 * mm});
            skCircle(sketch, "E3.0.11.21", {"center": v(15, 247.5) * mm, "radius": 10 * mm});
            skCircle(sketch, "E3.0.11.22", {"center": v(15, 272.5) * mm, "radius": 10 * mm});
            skCircle(sketch, "E3.0.12.10", {"center": v(45, -27.5) * mm, "radius": 10 * mm});
            skCircle(sketch, "E3.0.12.11", {"center": v(45, -2.5) * mm, "radius": 10 * mm});
            skCircle(sketch, "E3.0.12.12", {"center": v(45, 22.5) * mm, "radius": 10 * mm});
            skCircle(sketch, "E3.0.12.13", {"center": v(45, 47.5) * mm, "radius": 10 * mm});
            skCircle(sketch, "E3.0.12.14", {"center": v(45, 72.5) * mm, "radius": 10 * mm});
            skCircle(sketch, "E3.0.12.15", {"center": v(45, 97.5) * mm, "radius": 10 * mm});
            skCircle(sketch, "E3.0.12.16", {"center": v(45, 122.5) * mm, "radius": 10 * mm});
            skCircle(sketch, "E3.0.12.17", {"center": v(45, 147.5) * mm, "radius": 10 * mm});
            skCircle(sketch, "E3.0.12.18", {"center": v(45, 172.5) * mm, "radius": 10 * mm});
            skCircle(sketch, "E3.0.12.19", {"center": v(45, 197.5) * mm, "radius": 10 * mm});
            skCircle(sketch, "E3.0.12.20", {"center": v(45, 222.5) * mm, "radius": 10 * mm});
            skCircle(sketch, "E3.0.12.21", {"center": v(45, 247.5) * mm, "radius": 10 * mm});
            skCircle(sketch, "E3.0.12.22", {"center": v(45, 272.5) * mm, "radius": 10 * mm});
            skCircle(sketch, "E3.0.13.10", {"center": v(75, -27.5) * mm, "radius": 10 * mm});
            skCircle(sketch, "E3.0.13.11", {"center": v(75, -2.5) * mm, "radius": 10 * mm});
            skCircle(sketch, "E3.0.13.12", {"center": v(75, 22.5) * mm, "radius": 10 * mm});
            skCircle(sketch, "E3.0.13.13", {"center": v(75, 47.5) * mm, "radius": 10 * mm});
            skCircle(sketch, "E3.0.13.14", {"center": v(75, 72.5) * mm, "radius": 10 * mm});
            skCircle(sketch, "E3.0.13.15", {"center": v(75, 97.5) * mm, "radius": 10 * mm});
            skCircle(sketch, "E3.0.13.16", {"center": v(75, 122.5) * mm, "radius": 10 * mm});
            skCircle(sketch, "E3.0.13.17", {"center": v(75, 147.5) * mm, "radius": 10 * mm});
            skCircle(sketch, "E3.0.13.18", {"center": v(75, 172.5) * mm, "radius": 10 * mm});
            skCircle(sketch, "E3.0.13.19", {"center": v(75, 197.5) * mm, "radius": 10 * mm});
            skCircle(sketch, "E3.0.13.20", {"center": v(75, 222.5) * mm, "radius": 10 * mm});
            skCircle(sketch, "E3.0.13.21", {"center": v(75, 247.5) * mm, "radius": 10 * mm});
            skCircle(sketch, "E3.0.13.22", {"center": v(75, 272.5) * mm, "radius": 10 * mm});
            skCircle(sketch, "E3.0.14.10", {"center": v(105, -27.5) * mm, "radius": 10 * mm});
            skCircle(sketch, "E3.0.14.11", {"center": v(105, -2.5) * mm, "radius": 10 * mm});
            skCircle(sketch, "E3.0.14.12", {"center": v(105, 22.5) * mm, "radius": 10 * mm});
            skCircle(sketch, "E3.0.14.13", {"center": v(105, 47.5) * mm, "radius": 10 * mm});
            skCircle(sketch, "E3.0.14.14", {"center": v(105, 72.5) * mm, "radius": 10 * mm});
            skCircle(sketch, "E3.0.14.15", {"center": v(105, 97.5) * mm, "radius": 10 * mm});
            skCircle(sketch, "E3.0.14.16", {"center": v(105, 122.5) * mm, "radius": 10 * mm});
            skCircle(sketch, "E3.0.14.17", {"center": v(105, 147.5) * mm, "radius": 10 * mm});
            skCircle(sketch, "E3.0.14.18", {"center": v(105, 172.5) * mm, "radius": 10 * mm});
            skCircle(sketch, "E3.0.14.19", {"center": v(105, 197.5) * mm, "radius": 10 * mm});
            skCircle(sketch, "E3.0.14.20", {"center": v(105, 222.5) * mm, "radius": 10 * mm});
            skCircle(sketch, "E3.0.14.21", {"center": v(105, 247.5) * mm, "radius": 10 * mm});
            skCircle(sketch, "E3.0.14.22", {"center": v(105, 272.5) * mm, "radius": 10 * mm});
            skCircle(sketch, "E3.0.15.10", {"center": v(135, -27.5) * mm, "radius": 10 * mm});
            skCircle(sketch, "E3.0.15.11", {"center": v(135, -2.5) * mm, "radius": 10 * mm});
            skCircle(sketch, "E3.0.15.12", {"center": v(135, 22.5) * mm, "radius": 10 * mm});
            skCircle(sketch, "E3.0.15.13", {"center": v(135, 47.5) * mm, "radius": 10 * mm});
            skCircle(sketch, "E3.0.15.14", {"center": v(135, 72.5) * mm, "radius": 10 * mm});
            skCircle(sketch, "E3.0.15.15", {"center": v(135, 97.5) * mm, "radius": 10 * mm});
            skCircle(sketch, "E3.0.15.16", {"center": v(135, 122.5) * mm, "radius": 10 * mm});
            skCircle(sketch, "E3.0.15.17", {"center": v(135, 147.5) * mm, "radius": 10 * mm});
            skCircle(sketch, "E3.0.15.18", {"center": v(135, 172.5) * mm, "radius": 10 * mm});
            skCircle(sketch, "E3.0.15.19", {"center": v(135, 197.5) * mm, "radius": 10 * mm});
            skCircle(sketch, "E3.0.15.20", {"center": v(135, 222.5) * mm, "radius": 10 * mm});
            skCircle(sketch, "E3.0.15.21", {"center": v(135, 247.5) * mm, "radius": 10 * mm});
            skCircle(sketch, "E3.0.15.22", {"center": v(135, 272.5) * mm, "radius": 10 * mm});
            skCircle(sketch, "E3.0.16.10", {"center": v(165, -27.5) * mm, "radius": 10 * mm});
            skCircle(sketch, "E3.0.16.11", {"center": v(165, -2.5) * mm, "radius": 10 * mm});
            skCircle(sketch, "E3.0.16.12", {"center": v(165, 22.5) * mm, "radius": 10 * mm});
            skCircle(sketch, "E3.0.16.13", {"center": v(165, 47.5) * mm, "radius": 10 * mm});
            skCircle(sketch, "E3.0.16.14", {"center": v(165, 72.5) * mm, "radius": 10 * mm});
            skCircle(sketch, "E3.0.16.15", {"center": v(165, 97.5) * mm, "radius": 10 * mm});
            skCircle(sketch, "E3.0.16.16", {"center": v(165, 122.5) * mm, "radius": 10 * mm});
            skCircle(sketch, "E3.0.16.17", {"center": v(165, 147.5) * mm, "radius": 10 * mm});
            skCircle(sketch, "E3.0.16.18", {"center": v(165, 172.5) * mm, "radius": 10 * mm});
            skCircle(sketch, "E3.0.16.19", {"center": v(165, 197.5) * mm, "radius": 10 * mm});
            skCircle(sketch, "E3.0.16.20", {"center": v(165, 222.5) * mm, "radius": 10 * mm});
            skCircle(sketch, "E3.0.16.21", {"center": v(165, 247.5) * mm, "radius": 10 * mm});
            skCircle(sketch, "E3.0.16.22", {"center": v(165, 272.5) * mm, "radius": 10 * mm});
            skCircle(sketch, "E3.0.17.10", {"center": v(195, -27.5) * mm, "radius": 10 * mm});
            skCircle(sketch, "E3.0.17.11", {"center": v(195, -2.5) * mm, "radius": 10 * mm});
            skCircle(sketch, "E3.0.17.12", {"center": v(195, 22.5) * mm, "radius": 10 * mm});
            skCircle(sketch, "E3.0.17.13", {"center": v(195, 47.5) * mm, "radius": 10 * mm});
            skCircle(sketch, "E3.0.17.14", {"center": v(195, 72.5) * mm, "radius": 10 * mm});
            skCircle(sketch, "E3.0.17.15", {"center": v(195, 97.5) * mm, "radius": 10 * mm});
            skCircle(sketch, "E3.0.17.16", {"center": v(195, 122.5) * mm, "radius": 10 * mm});
            skCircle(sketch, "E3.0.17.17", {"center": v(195, 147.5) * mm, "radius": 10 * mm});
            skCircle(sketch, "E3.0.17.18", {"center": v(195, 172.5) * mm, "radius": 10 * mm});
            skCircle(sketch, "E3.0.17.19", {"center": v(195, 197.5) * mm, "radius": 10 * mm});
            skCircle(sketch, "E3.0.17.20", {"center": v(195, 222.5) * mm, "radius": 10 * mm});
            skCircle(sketch, "E3.0.17.21", {"center": v(195, 247.5) * mm, "radius": 10 * mm});
            skCircle(sketch, "E3.0.17.22", {"center": v(195, 272.5) * mm, "radius": 10 * mm});
            skCircle(sketch, "E3.0.18.10", {"center": v(225, -27.5) * mm, "radius": 10 * mm});
            skCircle(sketch, "E3.0.18.11", {"center": v(225, -2.5) * mm, "radius": 10 * mm});
            skCircle(sketch, "E3.0.18.12", {"center": v(225, 22.5) * mm, "radius": 10 * mm});
            skCircle(sketch, "E3.0.18.13", {"center": v(225, 47.5) * mm, "radius": 10 * mm});
            skCircle(sketch, "E3.0.18.14", {"center": v(225, 72.5) * mm, "radius": 10 * mm});
            skCircle(sketch, "E3.0.18.15", {"center": v(225, 97.5) * mm, "radius": 10 * mm});
            skCircle(sketch, "E3.0.18.16", {"center": v(225, 122.5) * mm, "radius": 10 * mm});
            skCircle(sketch, "E3.0.18.17", {"center": v(225, 147.5) * mm, "radius": 10 * mm});
            skCircle(sketch, "E3.0.18.18", {"center": v(225, 172.5) * mm, "radius": 10 * mm});
            skCircle(sketch, "E3.0.18.19", {"center": v(225, 197.5) * mm, "radius": 10 * mm});
            skCircle(sketch, "E3.0.18.20", {"center": v(225, 222.5) * mm, "radius": 10 * mm});
            skCircle(sketch, "E3.0.18.21", {"center": v(225, 247.5) * mm, "radius": 10 * mm});
            skCircle(sketch, "E3.0.18.22", {"center": v(225, 272.5) * mm, "radius": 10 * mm});
            skCircle(sketch, "E3.0.19.10", {"center": v(255, -27.5) * mm, "radius": 10 * mm});
            skCircle(sketch, "E3.0.19.11", {"center": v(255, -2.5) * mm, "radius": 10 * mm});
            skCircle(sketch, "E3.0.19.12", {"center": v(255, 22.5) * mm, "radius": 10 * mm});
            skCircle(sketch, "E3.0.19.13", {"center": v(255, 47.5) * mm, "radius": 10 * mm});
            skCircle(sketch, "E3.0.19.14", {"center": v(255, 72.5) * mm, "radius": 10 * mm});
            skCircle(sketch, "E3.0.19.15", {"center": v(255, 97.5) * mm, "radius": 10 * mm});
            skCircle(sketch, "E3.0.19.16", {"center": v(255, 122.5) * mm, "radius": 10 * mm});
            skCircle(sketch, "E3.0.19.17", {"center": v(255, 147.5) * mm, "radius": 10 * mm});
            skCircle(sketch, "E3.0.19.18", {"center": v(255, 172.5) * mm, "radius": 10 * mm});
            skCircle(sketch, "E3.0.19.19", {"center": v(255, 197.5) * mm, "radius": 10 * mm});
            skCircle(sketch, "E3.0.19.20", {"center": v(255, 222.5) * mm, "radius": 10 * mm});
            skCircle(sketch, "E3.0.19.21", {"center": v(255, 247.5) * mm, "radius": 10 * mm});
            skCircle(sketch, "E3.0.19.22", {"center": v(255, 272.5) * mm, "radius": 10 * mm});
            skCircle(sketch, "E4.0.20.0", {"center": v(285, -277.5) * mm, "radius": 10 * mm});
            skCircle(sketch, "E4.0.20.1", {"center": v(285, -252.5) * mm, "radius": 10 * mm});
            skCircle(sketch, "E4.0.20.2", {"center": v(285, -227.5) * mm, "radius": 10 * mm});
            skCircle(sketch, "E4.0.20.3", {"center": v(285, -202.5) * mm, "radius": 10 * mm});
            skCircle(sketch, "E4.0.20.4", {"center": v(285, -177.5) * mm, "radius": 10 * mm});
            skCircle(sketch, "E4.0.20.5", {"center": v(285, -152.5) * mm, "radius": 10 * mm});
            skCircle(sketch, "E4.0.20.6", {"center": v(285, -127.5) * mm, "radius": 10 * mm});
            skCircle(sketch, "E4.0.20.7", {"center": v(285, -102.5) * mm, "radius": 10 * mm});
            skCircle(sketch, "E4.0.20.8", {"center": v(285, -77.5) * mm, "radius": 10 * mm});
            skCircle(sketch, "E4.0.20.9", {"center": v(285, -52.5) * mm, "radius": 10 * mm});
            skCircle(sketch, "E4.0.20.10", {"center": v(285, -27.5) * mm, "radius": 10 * mm});
            skCircle(sketch, "E4.0.20.11", {"center": v(285, -2.5) * mm, "radius": 10 * mm});
            skCircle(sketch, "E4.0.20.12", {"center": v(285, 22.5) * mm, "radius": 10 * mm});
            skCircle(sketch, "E4.0.20.13", {"center": v(285, 47.5) * mm, "radius": 10 * mm});
            skCircle(sketch, "E4.0.20.14", {"center": v(285, 72.5) * mm, "radius": 10 * mm});
            skCircle(sketch, "E4.0.20.15", {"center": v(285, 97.5) * mm, "radius": 10 * mm});
            skCircle(sketch, "E4.0.20.16", {"center": v(285, 122.5) * mm, "radius": 10 * mm});
            skCircle(sketch, "E4.0.20.17", {"center": v(285, 147.5) * mm, "radius": 10 * mm});
            skCircle(sketch, "E4.0.20.18", {"center": v(285, 172.5) * mm, "radius": 10 * mm});
            skCircle(sketch, "E4.0.20.19", {"center": v(285, 197.5) * mm, "radius": 10 * mm});
            skCircle(sketch, "E4.0.20.20", {"center": v(285, 222.5) * mm, "radius": 10 * mm});
            skCircle(sketch, "E4.0.20.21", {"center": v(285, 247.5) * mm, "radius": 10 * mm});
            skCircle(sketch, "E4.0.20.22", {"center": v(285, 272.5) * mm, "radius": 10 * mm});
            skCircle(sketch, "E4.0.21.0", {"center": v(315, -277.5) * mm, "radius": 10 * mm});
            skCircle(sketch, "E4.0.21.1", {"center": v(315, -252.5) * mm, "radius": 10 * mm});
            skCircle(sketch, "E4.0.21.2", {"center": v(315, -227.5) * mm, "radius": 10 * mm});
            skCircle(sketch, "E4.0.21.3", {"center": v(315, -202.5) * mm, "radius": 10 * mm});
            skCircle(sketch, "E4.0.21.4", {"center": v(315, -177.5) * mm, "radius": 10 * mm});
            skCircle(sketch, "E4.0.21.5", {"center": v(315, -152.5) * mm, "radius": 10 * mm});
            skCircle(sketch, "E4.0.21.6", {"center": v(315, -127.5) * mm, "radius": 10 * mm});
            skCircle(sketch, "E4.0.21.7", {"center": v(315, -102.5) * mm, "radius": 10 * mm});
            skCircle(sketch, "E4.0.21.8", {"center": v(315, -77.5) * mm, "radius": 10 * mm});
            skCircle(sketch, "E4.0.21.9", {"center": v(315, -52.5) * mm, "radius": 10 * mm});
            skCircle(sketch, "E4.0.21.10", {"center": v(315, -27.5) * mm, "radius": 10 * mm});
            skCircle(sketch, "E4.0.21.11", {"center": v(315, -2.5) * mm, "radius": 10 * mm});
            skCircle(sketch, "E4.0.21.12", {"center": v(315, 22.5) * mm, "radius": 10 * mm});
            skCircle(sketch, "E4.0.21.13", {"center": v(315, 47.5) * mm, "radius": 10 * mm});
            skCircle(sketch, "E4.0.21.14", {"center": v(315, 72.5) * mm, "radius": 10 * mm});
            skCircle(sketch, "E4.0.21.15", {"center": v(315, 97.5) * mm, "radius": 10 * mm});
            skCircle(sketch, "E4.0.21.16", {"center": v(315, 122.5) * mm, "radius": 10 * mm});
            skCircle(sketch, "E4.0.21.17", {"center": v(315, 147.5) * mm, "radius": 10 * mm});
            skCircle(sketch, "E4.0.21.18", {"center": v(315, 172.5) * mm, "radius": 10 * mm});
            skCircle(sketch, "E4.0.21.19", {"center": v(315, 197.5) * mm, "radius": 10 * mm});
            skCircle(sketch, "E4.0.21.20", {"center": v(315, 222.5) * mm, "radius": 10 * mm});
            skCircle(sketch, "E4.0.21.21", {"center": v(315, 247.5) * mm, "radius": 10 * mm});
            skCircle(sketch, "E4.0.21.22", {"center": v(315, 272.5) * mm, "radius": 10 * mm});
            skSolve(sketch);
        }
        {
            var Q0;
            Q0=makeQuery(id+"F0.imprint","IMPRINT",FACE,{"disambiguationData":[TD([[makeQuery(id+"F0.imprint","IMPRINT",EDGE,{"derivedFrom":sQuery(id+"F0.wireOp",EDGE,"E0.bottom")}),-1.0]])]});
            extrude(context, id + "F1", {"entities" : qUnion([Q0]), "depth" : 2 * mm, "offsetDistance" : 25 * mm});
        }
    });
